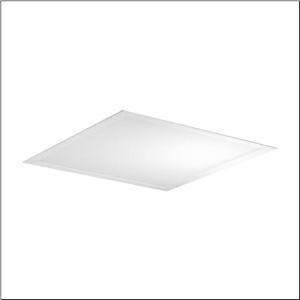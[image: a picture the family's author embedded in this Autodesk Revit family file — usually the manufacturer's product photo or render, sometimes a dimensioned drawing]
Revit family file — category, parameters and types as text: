
# Revit family: apollon_r__21_square_51mq11wd2454_78a7
name_source: partatom
category: Lighting Fixtures
units: mm (PartAtom-declared; Revit-internal decimal feet)

## family parameters
Cut with Voids When Loaded = No
Host = Face
Light Source = No
Part Type = Normal
Room Calculation Point = No
Round Connector Dimension = Use Diameter
Shared = No

## types (1)
- Apollon® 21 square (1 x LED, 4200 lm, 24.7 W, 4000K)
    Apparent Load = 25 VA
    CIE Flux Codes = 60 87 97 100 100
    Color Rendering = 80
    Color Temperature = 4000K
    Default Elevation = 1800 mm
    Description = Apollon® 21 square, office luminaire, primary optical cover: micro prismatic cover, of PMMA, CAT 2 (L<= 3000cd/m²), light emission: direct distribution, primary light characteristic: symmetric, installation type: lay-in mounting, LED, rated luminous flux: 4.200lm, luminous efficacy: 170lm/W, light colour: 840, colour temperature: 4000K, with terminal, 5-pole, mains connection: 220..240V, AC/DC, 0/50..60Hz, rated input power: 24.7W, housing, of aluminium, coated, traffic white (RAL 9016), module: M625, length: 620mm, width: 620mm, height: 30mm, housing upper side, of sheet steel, galvanised, protection rating (complete): IP20, protection rating (lamp compartment, on room side): IP54, insulation class (complete): insulation class II (safety insulation), certification: CE, ENEC, impact resistance: IK03, permissible operating ambient temperature: -20..+45°C, permissible storage temperature: -40..+80°C, packaging unit: 1 piece
    Height = 0 mm  [stored 0 ft]
    Lamp = 1 x LED
    Lamp Light Flux = 4200 lm
    Lamp Power = 24.7 W
    Lamp count = 1
    Length = 620 mm
    Luminous efficacy = 170 lm/W
    Manufacturer = Siteco
    ModVariant = No
    Model = 51MQ11WD2454
    Mounting Place = Ceiling
    Mounting Type = Recessed
    Number of Poles = 1
    OnlyDefault = Yes
    Power Factor = 1
    Product Name = Apollon® 21 square
    Product group = office luminaire | ceiling recessed
    ProductGroupID = 401
    Protection Class = Protection class II
    Protection Degree = IP 20
    RLX_Detail_Level = 1
    RLX_Emergency_Light_Flux = 0 lm
    RLX_Emergency_Type = 0
    RLX_Emergency_Type_DB = No
    RlxData = <blob elided: 12949 chars, md5=ef04f20f>
    Socket = socket
    Standby Power = 0 W
    System Light Flux = 4200 lm
    System Power = 25 W
    Type Comments = Product without accessories
    Type Image = l_1291054.jpg
    URL = http://relux.com
    VarID = ---
    Voltage = 0 V
    Weight = 0.00 kg
    Width = 620 mm

note: [stored X ft] marks values corroborated as IEEE doubles in the binary element streams (Revit-internal decimal feet)

## geometry (parser evidence)
native form markers: Sweep x9
no freeform markers — native parametric forms only
